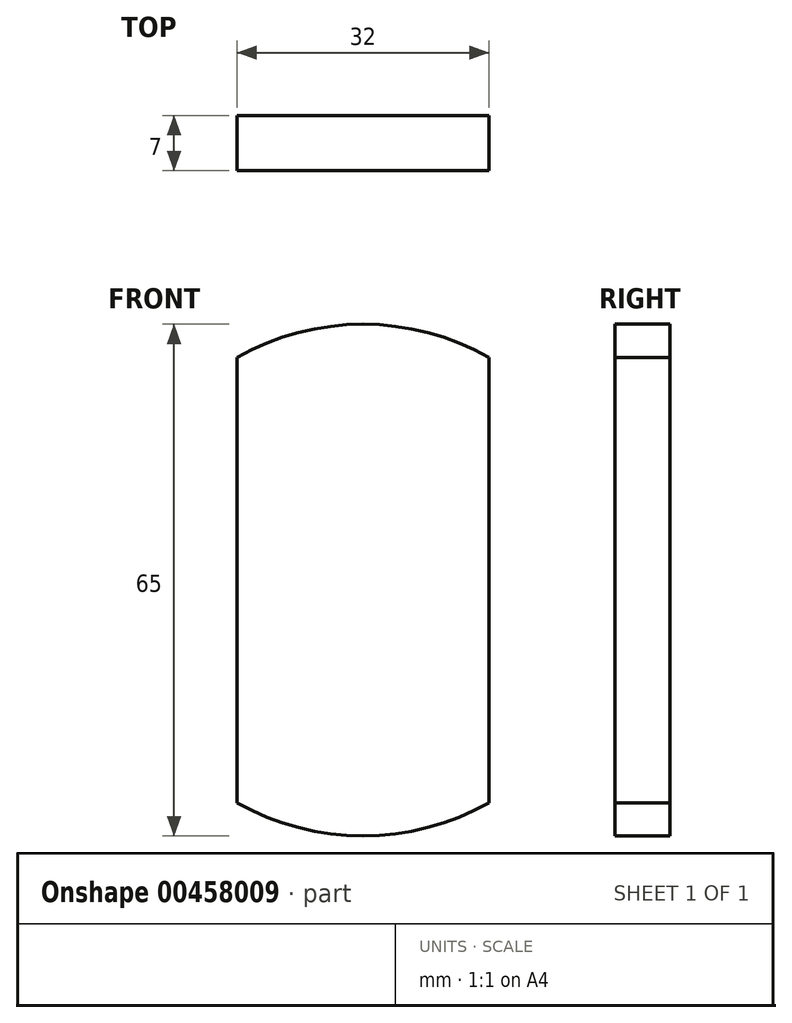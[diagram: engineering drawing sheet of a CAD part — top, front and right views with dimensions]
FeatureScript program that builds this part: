
annotation { "Feature Type Name" : "Feature", "Feature Type Description" : "" }
export const myFeature = defineFeature(function(context is Context, id is Id, definition is map)
    precondition{}
    {
        {
            var Q0;
            Q0=qCreatedBy(makeId("Front.planeOp"),FACE);
            var sketch = newSketch(context, id + "F0", { "sketchPlane" : qUnion([Q0])});
            skCircle(sketch, "E0", {"center": v(0, 0) * mm, "radius": 32.5 * mm});
            skLineSegment(sketch, "E1.bottom", {"start": v(16, -35) * mm, "end": v(-16, -35) * mm});
            skLineSegment(sketch, "E1.top", {"start": v(16, 35) * mm, "end": v(-16, 35) * mm});
            skLineSegment(sketch, "E1.left", {"start": v(16, -35) * mm, "end": v(16, 35) * mm});
            skLineSegment(sketch, "E1.right", {"start": v(-16, -35) * mm, "end": v(-16, 35) * mm});
            skLineSegment(sketch, "E2", {"start": v(-16, -7.5) * mm, "end": v(16, -7.5) * mm});
            skSolve(sketch);
        }
        {
            var Q0;
            {var subQ0=sQuery(id+"F0.wireOp",EDGE,"E1.right");var subQ1=sQuery(id+"F0.wireOp",EDGE,"E0");var subQ2=makeQuery(id+"F0.imprint","INTERSECT",VERTEX,{"disambiguationData":[OD(0.0)],"derivedFrom":[subQ1,subQ0]});Q0=makeQuery(id+"F0.imprint","IMPRINT",FACE,{"disambiguationData":[TD([[makeQuery(id+"F0.imprint","IMPRINT",EDGE,{"disambiguationData":[TD([[subQ2,-1.0]])],"derivedFrom":subQ1}),1.0]])]});}
            var Q1;
            {var subQ5=sQuery(id+"F0.wireOp",EDGE,"E2");Q1=makeQuery(id+"F0.imprint","IMPRINT",FACE,{"disambiguationData":[TD([[makeQuery(id+"F0.imprint","IMPRINT",EDGE,{"derivedFrom":subQ5}),1.0]])]});}
            var Q2;
            {var subQ0=sQuery(id+"F0.wireOp",EDGE,"E1.left");var subQ1=sQuery(id+"F0.wireOp",EDGE,"E0");var subQ2=makeQuery(id+"F0.imprint","INTERSECT",VERTEX,{"disambiguationData":[OD(0.0)],"derivedFrom":[subQ1,subQ0]});Q2=makeQuery(id+"F0.imprint","IMPRINT",FACE,{"disambiguationData":[TD([[makeQuery(id+"F0.imprint","IMPRINT",EDGE,{"disambiguationData":[TD([[subQ2,1.0]])],"derivedFrom":subQ1}),1.0]])]});}
            extrude(context, id + "F1", {"entities" : qUnion([Q0, Q1, Q2]), "depth" : 7 * mm});
        }
    });
